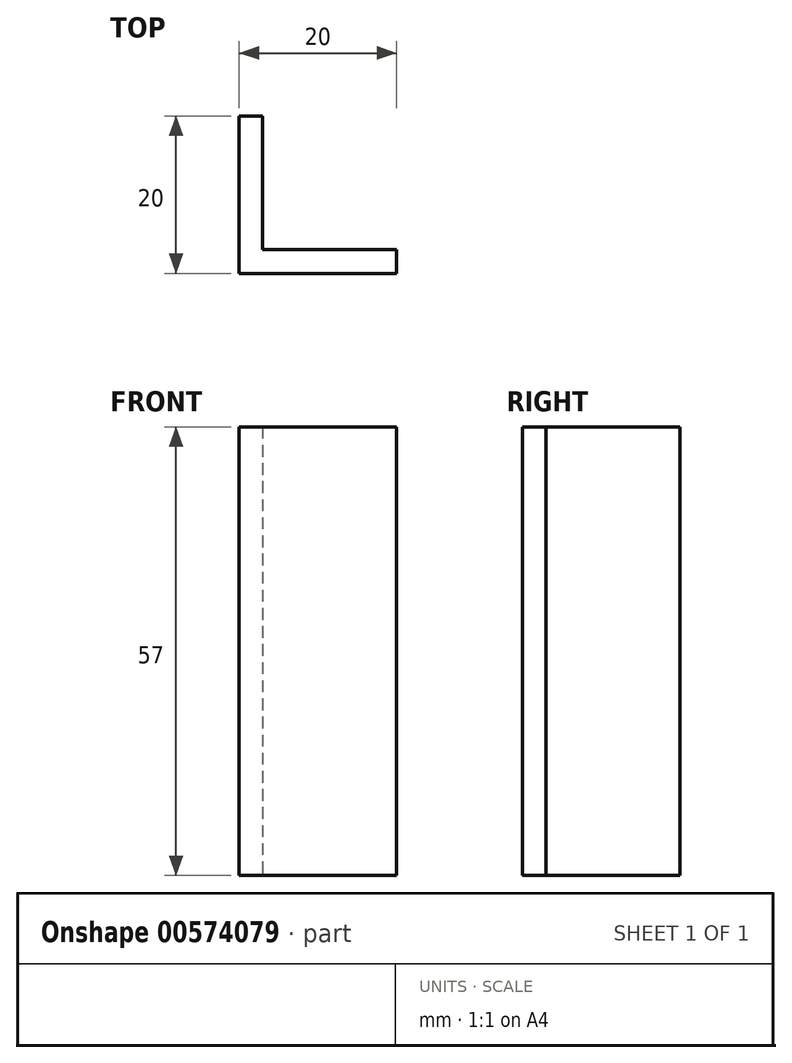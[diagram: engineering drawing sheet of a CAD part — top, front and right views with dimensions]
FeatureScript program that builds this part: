
annotation { "Feature Type Name" : "Feature", "Feature Type Description" : "" }
export const myFeature = defineFeature(function(context is Context, id is Id, definition is map)
    precondition{}
    {
        {
            var Q0;
            Q0=qCreatedBy(makeId("Top.planeOp"),FACE);
            var sketch = newSketch(context, id + "F0", { "sketchPlane" : qUnion([Q0])});
            skLineSegment(sketch, "E0.bottom", {"start": v(0, 0) * mm, "end": v(20, 0) * mm});
            skLineSegment(sketch, "E0.top", {"start": v(0, 20) * mm, "end": v(3, 20) * mm});
            skLineSegment(sketch, "E0.left", {"start": v(0, 0) * mm, "end": v(0, 20) * mm});
            skLineSegment(sketch, "E0.right", {"start": v(20, 0) * mm, "end": v(20, 3) * mm});
            skLineSegment(sketch, "E1.top", {"start": v(20, 3) * mm, "end": v(3, 3) * mm});
            skLineSegment(sketch, "E1.right", {"start": v(3, 20) * mm, "end": v(3, 3) * mm});
            skSolve(sketch);
        }
        {
            var Q0;
            Q0=makeQuery(id+"F0.imprint","IMPRINT",FACE,{"disambiguationData":[TD([[makeQuery(id+"F0.imprint","IMPRINT",EDGE,{"derivedFrom":sQuery(id+"F0.wireOp",EDGE,"E0.bottom")}),1.0]])]});
            extrude(context, id + "F1", {"entities" : qUnion([Q0]), "depth" : 57 * mm, "offsetDistance" : 25 * mm});
        }
    });
